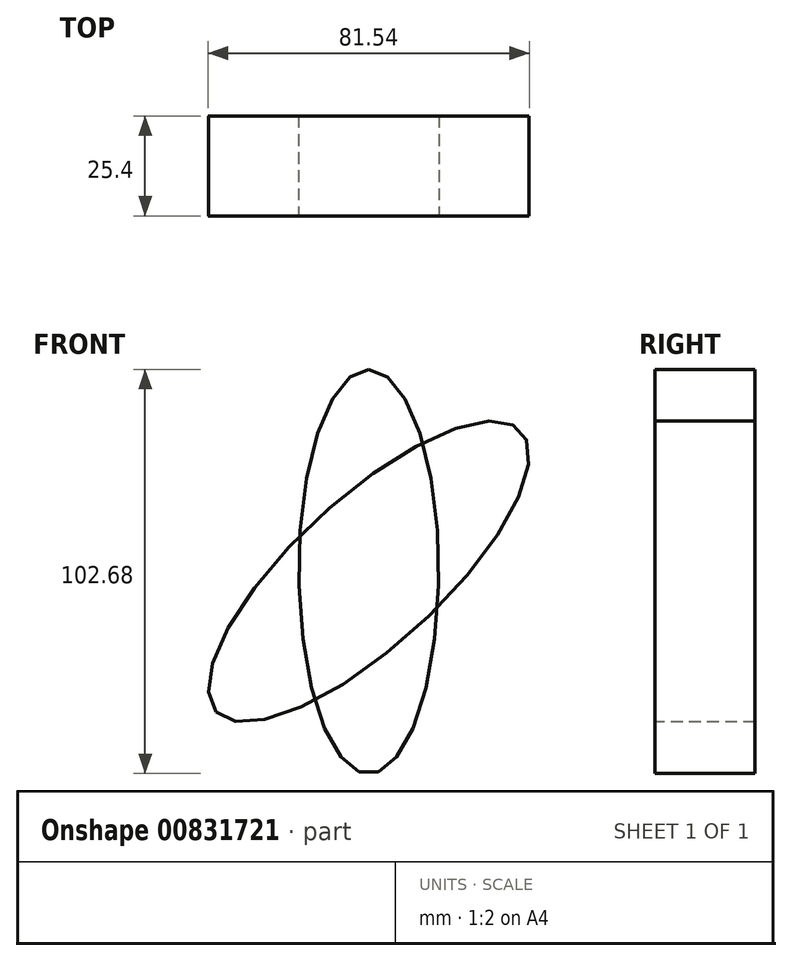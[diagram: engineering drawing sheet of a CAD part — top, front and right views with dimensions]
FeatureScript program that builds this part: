
annotation { "Feature Type Name" : "Feature", "Feature Type Description" : "" }
export const myFeature = defineFeature(function(context is Context, id is Id, definition is map)
    precondition{}
    {
        {
            var Q0;
            Q0=qCreatedBy(makeId("Front.planeOp"),FACE);
            var sketch = newSketch(context, id + "F0", { "sketchPlane" : qUnion([Q0])});
            skEllipse(sketch, "E0", {"center": v(0, 0) * mm, "majorRadius": 51.34 * mm, "minorRadius": 17.79 * mm, "majorAxis": v(0, 1)});
            skSolve(sketch);
        }
        {
            var Q0;
            Q0=sQuery(id+"F0.wireOp",EDGE,"E0");
            extrude(context, id + "F1", {"bodyType" : ToolBodyType.SURFACE, "surfaceEntities" : qUnion([Q0]), "depth" : 25.4 * mm, "offsetDistance" : 25.4 * mm});
        }
        {
            var Q0;
            Q0=qCreatedBy(makeId("Front.planeOp"),FACE);
            var sketch = newSketch(context, id + "F2", { "sketchPlane" : qUnion([Q0])});
            skEllipse(sketch, "E1", {"center": v(0, 0) * mm, "majorRadius": 52.66 * mm, "minorRadius": 18.72 * mm, "majorAxis": v(-0.74, -0.68)});
            skSolve(sketch);
        }
        {
            var Q0;
            Q0=sQuery(id+"F2.wireOp",EDGE,"E1");
            extrude(context, id + "F3", {"bodyType" : ToolBodyType.SURFACE, "surfaceEntities" : qUnion([Q0]), "depth" : 25.4 * mm, "offsetDistance" : 25.4 * mm});
        }
    });
